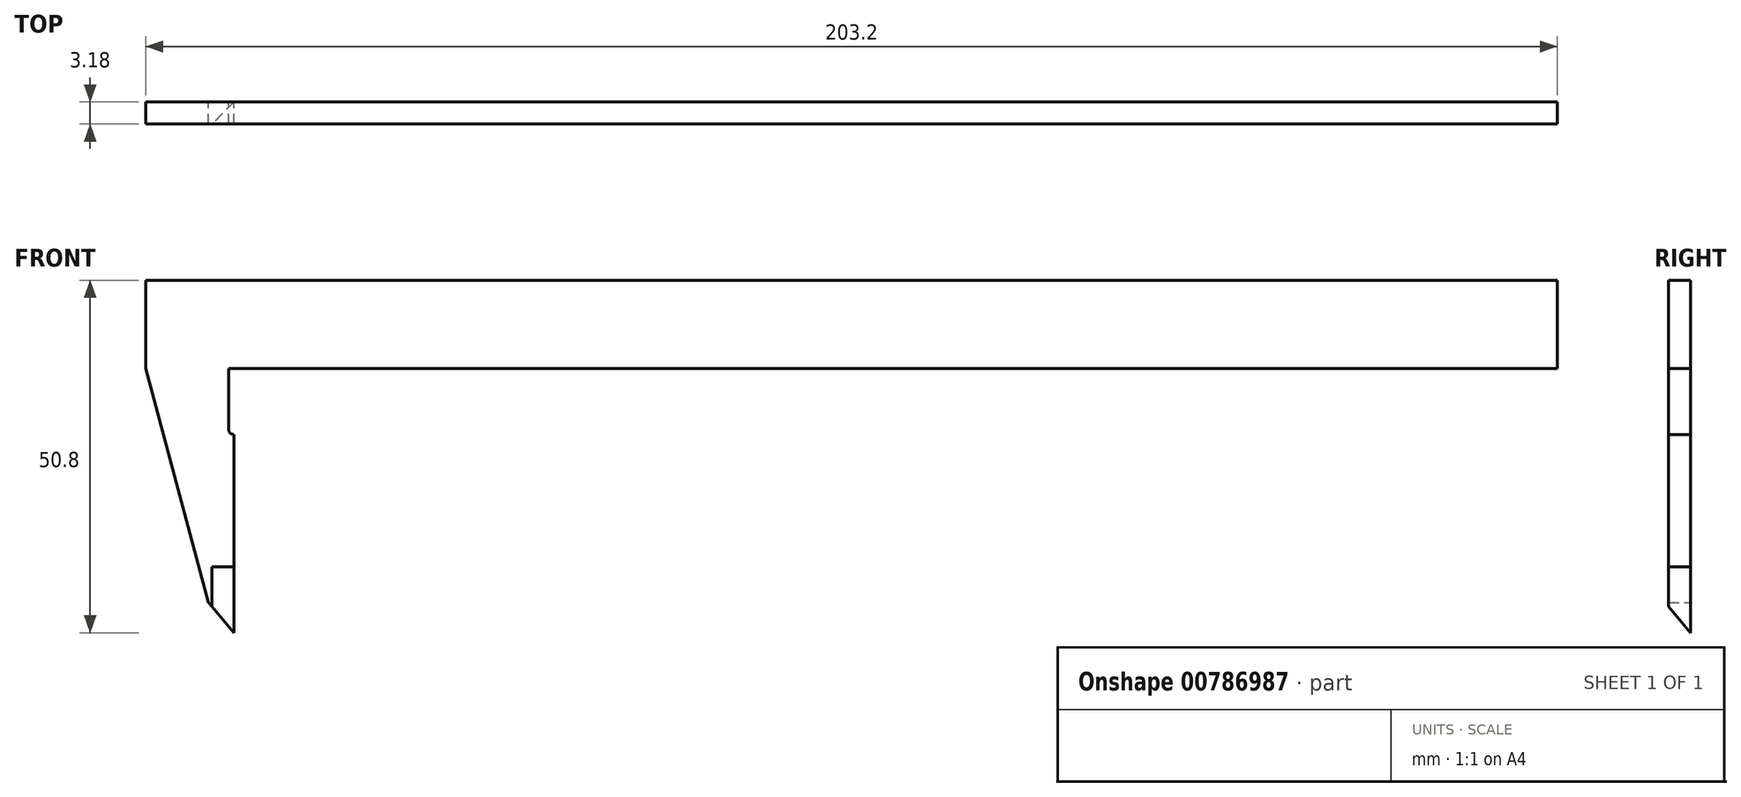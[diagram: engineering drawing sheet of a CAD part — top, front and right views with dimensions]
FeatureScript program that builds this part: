
annotation { "Feature Type Name" : "Feature", "Feature Type Description" : "" }
export const myFeature = defineFeature(function(context is Context, id is Id, definition is map)
    precondition{}
    {
        {
            var Q0;
            Q0=qCreatedBy(makeId("Front.planeOp"),FACE);
            var sketch = newSketch(context, id + "F0", { "sketchPlane" : qUnion([Q0])});
            skLineSegment(sketch, "E0.bottom", {"start": v(-101.6, 6.35) * mm, "end": v(101.6, 6.35) * mm});
            skLineSegment(sketch, "E0.top", {"start": v(-89.69, -6.35) * mm, "end": v(101.6, -6.35) * mm});
            skLineSegment(sketch, "E0.left", {"start": v(-101.6, 6.35) * mm, "end": v(-101.6, -6.35) * mm});
            skLineSegment(sketch, "E0.right", {"start": v(101.6, 6.35) * mm, "end": v(101.6, -6.35) * mm});
            skPoint(sketch, "E0.middle", {"position": v(0, 0) * mm});
            skLineSegment(sketch, "E1", {"start": v(-89.69, -6.35) * mm, "end": v(-89.69, -15.09) * mm});
            skLineSegment(sketch, "E2", {"start": v(-88.9, -15.87) * mm, "end": v(-88.9, -34.92) * mm});
            skArc(sketch, "E3", {"start": v(-89.69, -15.09) * mm, "mid": v(-89.46, -15.64) * mm, "end": v(-88.9, -15.87) * mm});
            skLineSegment(sketch, "E4", {"start": v(-101.6, -6.35) * mm, "end": v(-92.56, -40.09) * mm});
            skLineSegment(sketch, "E5", {"start": v(-92.56, -40.09) * mm, "end": v(-92.08, -40.67) * mm});
            skLineSegment(sketch, "E6", {"start": v(-88.9, -34.92) * mm, "end": v(-92.08, -34.92) * mm});
            skLineSegment(sketch, "E7", {"start": v(-92.08, -34.92) * mm, "end": v(-92.08, -40.67) * mm});
            skPoint(sketch, "E8.orphan", {"position": v(-88.9, -44.45) * mm});
            skSolve(sketch);
        }
        {
            var Q0;
            Q0=makeQuery(id+"F0.imprint","IMPRINT",FACE,{"disambiguationData":[TD([[makeQuery(id+"F0.imprint","IMPRINT",EDGE,{"derivedFrom":sQuery(id+"F0.wireOp",EDGE,"E0.bottom")}),-1.0]])]});
            var Q1;
            {var subQ3=sQuery(id+"F0.wireOp",EDGE,"LKpaG6vd-v6SP-MXo2-UOo8-r8vcHRsFXX15");Q1=makeQuery(id+"F0.imprint","IMPRINT",FACE,{"disambiguationData":[TD([[makeQuery(id+"F0.imprint","IMPRINT",EDGE,{"derivedFrom":subQ3}),1.0]])]});}
            extrude(context, id + "F1", {"entities" : qUnion([Q0, Q1]), "depth" : 3.17 * mm, "offsetDistance" : 25.4 * mm});
        }
        {
            var Q0;
            Q0=makeQuery(id+"F1.opExtrude","SWEPT_FACE",FACE,{"disambiguationData":[OSD([sQuery(id+"F0.wireOp",EDGE,"E6")])]});
            var sketch = newSketch(context, id + "F2", { "sketchPlane" : qUnion([Q0])});
            skLineSegment(sketch, "E9", {"start": v(-92.08, 3.17) * mm, "end": v(-88.9, 0) * mm});
            skSolve(sketch);
        }
        {
            var Q0;
            Q0=makeQuery(id+"F2.imprint","IMPRINT",FACE,{"disambiguationData":[TD([[makeQuery(id+"F2.imprint","IMPRINT",EDGE,{"derivedFrom":sQuery(id+"F2.wireOp",EDGE,"E9")}),-1.0]])]});
            extrude(context, id + "F3", {"entities" : qUnion([Q0]), "operationType" : NewBodyOperationType.ADD, "depth" : 9.52 * mm, "offsetDistance" : 25.4 * mm});
        }
        {
            var Q0;
            {var subQ0=sQuery(id+"F0.wireOp",EDGE,"E6");Q0=makeQuery(id+"F3.boolean.opBoolean","MERGE",FACE,{"derivedFrom":[makeQuery(id+"F1.opExtrude","CAP_FACE",FACE,{"disambiguationData":[OSD([sQuery(id+"F0.wireOp",EDGE,"E0.bottom"),sQuery(id+"F0.wireOp",EDGE,"E0.top"),sQuery(id+"F0.wireOp",EDGE,"E0.left"),sQuery(id+"F0.wireOp",EDGE,"E0.right"),sQuery(id+"F0.wireOp",EDGE,"E1"),sQuery(id+"F0.wireOp",EDGE,"E2"),sQuery(id+"F0.wireOp",EDGE,"E3"),sQuery(id+"F0.wireOp",EDGE,"E4"),sQuery(id+"F0.wireOp",EDGE,"E5"),subQ0,sQuery(id+"F0.wireOp",EDGE,"E7")])],"isStart":true}),makeQuery(id+"F3.opExtrude","SWEPT_FACE",FACE,{"disambiguationData":[OSD([subQ0])]})]});}
            var sketch = newSketch(context, id + "F4", { "sketchPlane" : qUnion([Q0])});
            skLineSegment(sketch, "E10", {"start": v(92.08, -40.67) * mm, "end": v(88.9, -44.45) * mm});
            skSolve(sketch);
        }
        {
            var Q0;
            Q0=makeQuery(id+"F4.imprint","IMPRINT",FACE,{"disambiguationData":[TD([[makeQuery(id+"F4.imprint","IMPRINT",EDGE,{"derivedFrom":sQuery(id+"F4.wireOp",EDGE,"E10")}),1.0]])]});
            extrude(context, id + "F5", {"entities" : qUnion([Q0]), "operationType" : NewBodyOperationType.REMOVE, "endBound" : BoundingType.THROUGH_ALL, "oppositeDirection" : true, "depth" : 25.4 * mm, "offsetDistance" : 25.4 * mm});
        }
    });
